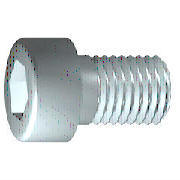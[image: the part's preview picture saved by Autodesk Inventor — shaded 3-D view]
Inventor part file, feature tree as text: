
AUTODESK INVENTOR PART (.ipt)
format: ipt  version: 2024.3 (Build 283343000, 343)  size: 188,928 bytes
history: native  units: mm (DEFAULTED — no unit token found)
features: extrude x1, plane x1, fillet x1
ambient origin geometry x7: Origin, YZ Plane, XY Plane, X Axis, Y Axis, Z Axis, Center Point
bodies: Solid1 (feature_tree), Body (feature_tree)
feature tree (3):
  extrude  "Slot"  Depth=23.25mm
  plane  "Work Plane1"
  fillet  "Fillet2"  Radius=0.429515mm
